# Revit family: NBS_DudleyIndustriesLimited_BthrmCbnts_ModuloSlimlineBehindTheMirrorHandHygieneSystemBaseShelf_92405BK
name_source: partatom
category: Casework
units: mm (PartAtom-declared; Revit-internal decimal feet)

## family parameters
Always vertical = Yes
Cut with Voids When Loaded = No
Room Calculation Point = No
Shared = No
Work Plane-Based = No

## types (1)
- 92405BK Modulo Slimline Base Shelf
    AssetType = Fixed
    BIMObjectName = NBS_DudleyIndustriesLimited_BathroomCabinets_ModuloSlimlineBehindTheMirrorHandHygieneSystemBaseShelf_92405BK
    BlankingPlates = Not required.,Required
    CarcassFinishAndColour = Matte black powder coated
    CarcassMaterials = Stainless steel
    Category = Pr_40_30_87_03:Bathroom cabinets
    Color = Black
    Description = Bathroom cabinet
    DurationUnit = year
    Finish = Powder-coated
    Form = Fixed to wall bracket
    IfcExportAs = IfcFurnitureType
    IfcExportType = NOTDEFINED
    IntegralAccessories = Hairdryers.,Paper towel dispenser.,Soap dispensers
    ManufacturerName = Dudley Industries Limited
    ManufacturerURL = www.dudleyindustries.com
    Material = Stainless steel
    ModelReference = 92405BK Modulo Slimline Base Shelf
    NBSCertification = www.nationalbimlibrary.com/cert/wzwjwmn2
    Name = BathroomCabinets_ModuloSlimlineBehindTheMirrorHandHygieneSystemBaseShelf_92405BK_DudleyIndustriesLimited
    NominalHeight = 75 mm
    NominalLength = 0 mm  [stored 0 ft]
    NominalWidth = 596 mm  [stored 1.95538 ft]
    Shape = Rectangle
    ShelfDepth = 212 mm  [stored 0.695538 ft]
    ShelfHeight = 75 mm
    ShelfMaterial = NBS_DudleyIndustriesLimited_StainlessSteel_MatteBlackPowderCoated
    ShelfWidth = 596 mm  [stored 1.95538 ft]
    Size = 596 x 75 x 212 mm
    SizeNominal = 596 x 75 x 212 mm
    Uniclass2015Code = Pr_40_30_87_03
    Uniclass2015Title = Bathroom cabinets
    Uniclass2015Version = Products v1.22
    Version = 1
    WarrantyDescription = Ten year
    WarrantyDurationUnit = year

note: [stored X ft] marks values corroborated as IEEE doubles in the binary element streams (Revit-internal decimal feet)

## geometry (parser evidence)
native form markers: Sweep x2
no freeform markers — native parametric forms only
